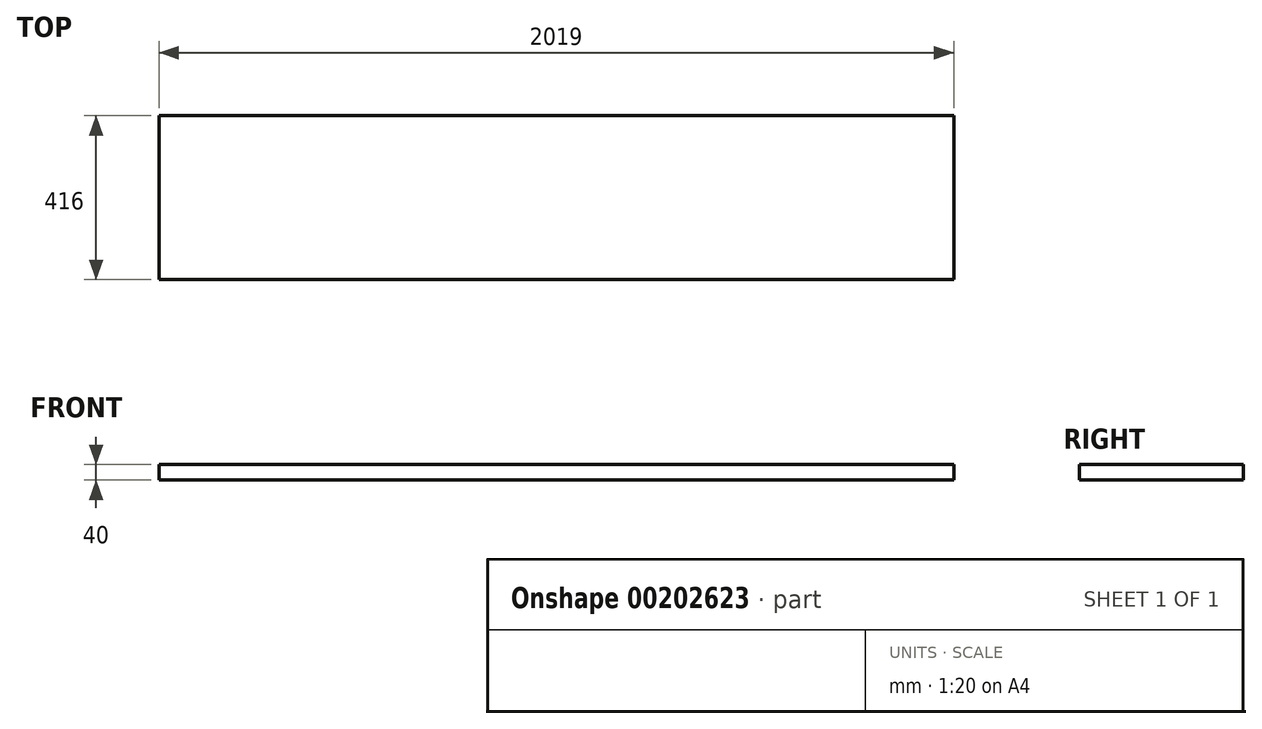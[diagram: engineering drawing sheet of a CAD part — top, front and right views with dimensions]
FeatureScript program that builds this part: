
annotation { "Feature Type Name" : "Feature", "Feature Type Description" : "" }
export const myFeature = defineFeature(function(context is Context, id is Id, definition is map)
    precondition{}
    {
        {
            var Q0;
            Q0=qCreatedBy(makeId("Top.planeOp"),FACE);
            var sketch = newSketch(context, id + "F0", { "sketchPlane" : qUnion([Q0])});
            skLineSegment(sketch, "E0.bottom", {"start": v(-864.34, -235.28) * mm, "end": v(1154.66, -235.28) * mm});
            skLineSegment(sketch, "E0.top", {"start": v(-864.34, 180.72) * mm, "end": v(1154.66, 180.72) * mm});
            skLineSegment(sketch, "E0.left", {"start": v(-864.34, -235.28) * mm, "end": v(-864.34, 180.72) * mm});
            skLineSegment(sketch, "E0.right", {"start": v(1154.66, -235.28) * mm, "end": v(1154.66, 180.72) * mm});
            skSolve(sketch);
        }
        {
            var Q0;
            Q0=makeQuery(id+"F0.imprint","IMPRINT",FACE,{"disambiguationData":[TD([[makeQuery(id+"F0.imprint","IMPRINT",EDGE,{"derivedFrom":sQuery(id+"F0.wireOp",EDGE,"E0.bottom")}),1.0]])]});
            extrude(context, id + "F1", {"entities" : qUnion([Q0]), "depth" : 40 * mm});
        }
    });
